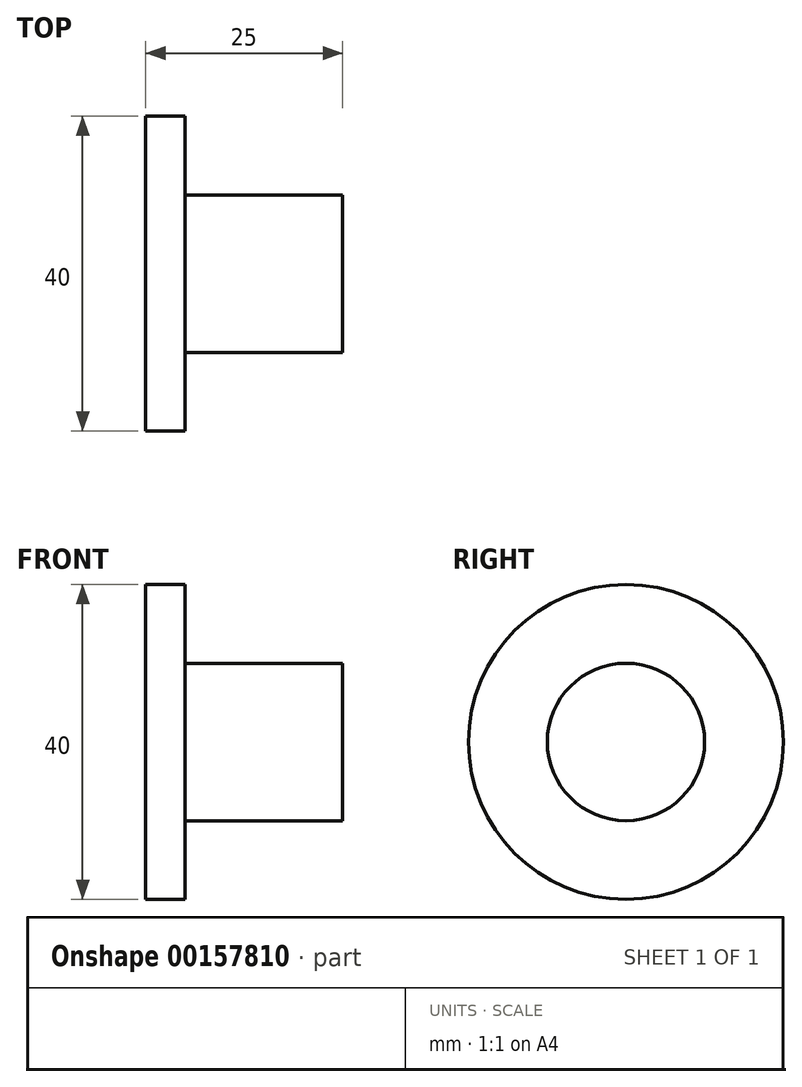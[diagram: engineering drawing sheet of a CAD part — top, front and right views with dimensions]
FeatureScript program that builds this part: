
annotation { "Feature Type Name" : "Feature", "Feature Type Description" : "" }
export const myFeature = defineFeature(function(context is Context, id is Id, definition is map)
    precondition{}
    {
        {
            var Q0;
            Q0=qCreatedBy(makeId("Top.planeOp"),FACE);
            var sketch = newSketch(context, id + "F0", { "sketchPlane" : qUnion([Q0])});
            skLineSegment(sketch, "E0", {"start": v(0, 0) * mm, "end": v(0, 20) * mm});
            skLineSegment(sketch, "E1", {"start": v(0, 20) * mm, "end": v(5, 20) * mm});
            skLineSegment(sketch, "E2", {"start": v(5, 20) * mm, "end": v(5, 10) * mm});
            skLineSegment(sketch, "E3", {"start": v(5, 10) * mm, "end": v(25, 10) * mm});
            skLineSegment(sketch, "E4", {"start": v(25, 10) * mm, "end": v(25, 0) * mm});
            skLineSegment(sketch, "E5", {"start": v(25, 0) * mm, "end": v(0, 0) * mm});
            skSolve(sketch);
        }
        {
            var Q0;
            Q0=makeQuery(id+"F0.imprint","IMPRINT",FACE,{"disambiguationData":[TD([[makeQuery(id+"F0.imprint","IMPRINT",EDGE,{"derivedFrom":sQuery(id+"F0.wireOp",EDGE,"E0")}),-1.0]])]});
            var Q1;
            Q1=sQuery(id+"F0.wireOp",EDGE,"E5");
            revolve(context, id + "F1", {"entities" : qUnion([Q0]), "axis" : qUnion([Q1]), "revolveType" : RevolveType.FULL});
        }
    });
